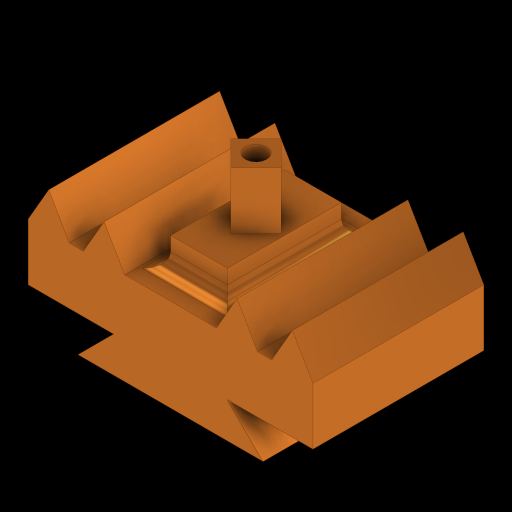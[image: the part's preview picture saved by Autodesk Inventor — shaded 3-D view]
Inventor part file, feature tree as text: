
AUTODESK INVENTOR PART (.ipt)
format: ipt  version: 2024 (Build 280153000, 153)  size: 226,304 bytes
history: native  units: in
note: dims shown in document units (in); Inventor stores cm internally (conversion verified against a paired STEP export)
features: sketch x4, extrude x3, hole x1, fillet x1
ambient origin geometry x8: Origin, YZ Plane, XZ Plane, XY Plane, X Axis, Y Axis, Z Axis, Center Point
bodies: Solid1 (feature_tree)
feature tree (9):
  extrude  "MAIN BODY"  TaperAngle=45.0deg  [1 undecoded]
  extrude  "LARGE BOSS"  TaperAngle=60.0deg  [1 undecoded]
  extrude  "TALL BOSS"  Depth=1.0in
  hole  "THROUGH HOLE"  [1 undecoded]
  fillet  "LARGE BOSS FILLET"  Radius=0.625in
  sketch  "Sketch1"  dims[d0=45.0deg d1=45.0deg]
  sketch  "Sketch2"  dims[d2=5.0in d3=60.0deg]
  sketch  "Sketch3"  dims[d4=0.25in d5=1.0in]
  sketch  "Sketch4"  dims[d6=1.0in d7=1.5in d8=0.625in d9=0.25in d10=60.0deg d11=60.0deg d12=60.0deg d13=1.0in d14=1.0in d15=1.0in d16=0.625in d17=60.0deg d20=3.0in d21=0.0in d25=2.0in d26=1.0in d27=0.5in d28=1.6132in d29=0.3066in d30=3.0in d32=0.5in d33=0.0in d34=0.625in d35=0.625in d36=45.0deg d39=1.0in d40=0.0in d41=0.375in d42=0.75in d43=0.375in d44=0.25in d45=0.5635in d46=1.0in d47=0.8108in d49=0.25in d37=0.0344in]
note: 3 required parameter values undecoded (feature->parameter linkage not recoverable at this tier; creation-order binding heuristic only, values carry confidence <= 0.55)
